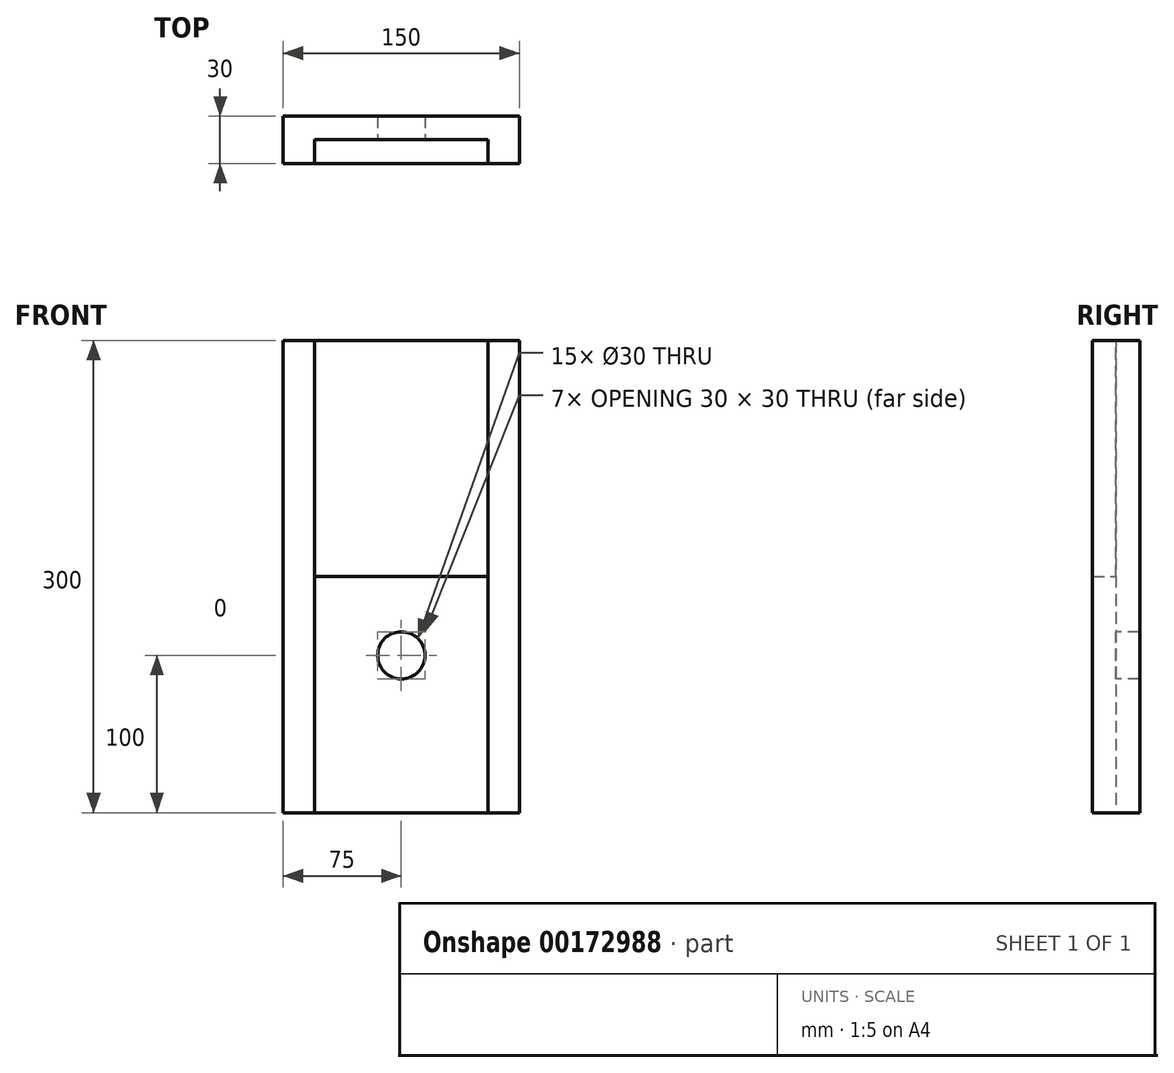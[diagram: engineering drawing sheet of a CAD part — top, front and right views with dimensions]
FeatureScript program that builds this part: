
annotation { "Feature Type Name" : "Feature", "Feature Type Description" : "" }
export const myFeature = defineFeature(function(context is Context, id is Id, definition is map)
    precondition{}
    {
        {
            var Q0;
            Q0=qCreatedBy(makeId("Top.planeOp"),FACE);
            var sketch = newSketch(context, id + "F0", { "sketchPlane" : qUnion([Q0])});
            skLineSegment(sketch, "E0", {"start": v(55, 0) * mm, "end": v(55, 15) * mm});
            skLineSegment(sketch, "E1", {"start": v(55, 15) * mm, "end": v(0, 15) * mm});
            skLineSegment(sketch, "E2", {"start": v(0, 15) * mm, "end": v(0, 30) * mm});
            skLineSegment(sketch, "E3", {"start": v(0, 30) * mm, "end": v(75, 30) * mm});
            skLineSegment(sketch, "E4", {"start": v(75, 30) * mm, "end": v(75, 0) * mm});
            skLineSegment(sketch, "E5", {"start": v(75, 0) * mm, "end": v(55, 0) * mm});
            skLineSegment(sketch, "E6", {"start": v(0, 0) * mm, "end": v(0, 30) * mm, "construction": true});
            skLineSegment(sketch, "E7.MirrorCS", {"start": v(0, 30) * mm, "end": v(-75, 30) * mm});
            skLineSegment(sketch, "E8.MirrorCS", {"start": v(-55, 15) * mm, "end": v(0, 15) * mm});
            skLineSegment(sketch, "E9.MirrorCS", {"start": v(-55, 0) * mm, "end": v(-55, 15) * mm});
            skLineSegment(sketch, "E10.MirrorCS", {"start": v(-75, 0) * mm, "end": v(-55, 0) * mm});
            skLineSegment(sketch, "E11.MirrorCS", {"start": v(-75, 30) * mm, "end": v(-75, 0) * mm});
            skSolve(sketch);
        }
        {
            var Q0;
            Q0 = qSketchRegion(id + "F0", true);
            extrude(context, id + "F1", {"entities" : qUnion([Q0]), "depth" : 200 * mm, "hasSecondDirection" : true, "secondDirectionOppositeDirection" : true, "secondDirectionDepth" : 100 * mm});
        }
        {
            var Q0;
            Q0=makeQuery(id+"F1.opExtrude","SWEPT_FACE",FACE,{"disambiguationData":[OSD([sQuery(id+"F0.wireOp",EDGE,"E1"),sQuery(id+"F0.wireOp",EDGE,"E8.MirrorCS")])]});
            var sketch = newSketch(context, id + "F2", { "sketchPlane" : qUnion([Q0])});
            skCircle(sketch, "E12", {"center": v(0, 0) * mm, "radius": 15 * mm});
            skSolve(sketch);
        }
        {
            var Q0;
            Q0=makeQuery(id+"F2.imprint","IMPRINT",FACE,{"disambiguationData":[TD([[makeQuery(id+"F2.imprint","IMPRINT",EDGE,{"derivedFrom":sQuery(id+"F2.wireOp",EDGE,"E12")}),1.0]])]});
            extrude(context, id + "F3", {"entities" : qUnion([Q0]), "operationType" : NewBodyOperationType.REMOVE, "oppositeDirection" : true, "depth" : 20 * mm});
        }
        {
            var Q0;
            Q0=makeQuery(id+"F1.opExtrude","CAP_FACE",FACE,{"disambiguationData":[OSD([sQuery(id+"F0.wireOp",EDGE,"E0"),sQuery(id+"F0.wireOp",EDGE,"E1"),sQuery(id+"F0.wireOp",EDGE,"E3"),sQuery(id+"F0.wireOp",EDGE,"E4"),sQuery(id+"F0.wireOp",EDGE,"E5"),sQuery(id+"F0.wireOp",EDGE,"E7.MirrorCS"),sQuery(id+"F0.wireOp",EDGE,"E8.MirrorCS"),sQuery(id+"F0.wireOp",EDGE,"E9.MirrorCS"),sQuery(id+"F0.wireOp",EDGE,"E10.MirrorCS"),sQuery(id+"F0.wireOp",EDGE,"E11.MirrorCS")])],"isStart":false});
            var sketch = newSketch(context, id + "F4", { "sketchPlane" : qUnion([Q0])});
            skLineSegment(sketch, "E13", {"start": v(-55, 0) * mm, "end": v(-55, 15) * mm});
            skLineSegment(sketch, "E14", {"start": v(-55, 15) * mm, "end": v(55, 15) * mm});
            skLineSegment(sketch, "E15", {"start": v(55, 15) * mm, "end": v(55, 0) * mm});
            skLineSegment(sketch, "E16", {"start": v(55, 0) * mm, "end": v(-55, 0) * mm});
            skSolve(sketch);
        }
        {
            var Q0;
            Q0 = qSketchRegion(id + "F4", true);
            extrude(context, id + "F5", {"entities" : qUnion([Q0]), "oppositeDirection" : true, "depth" : 150 * mm});
        }
    });
